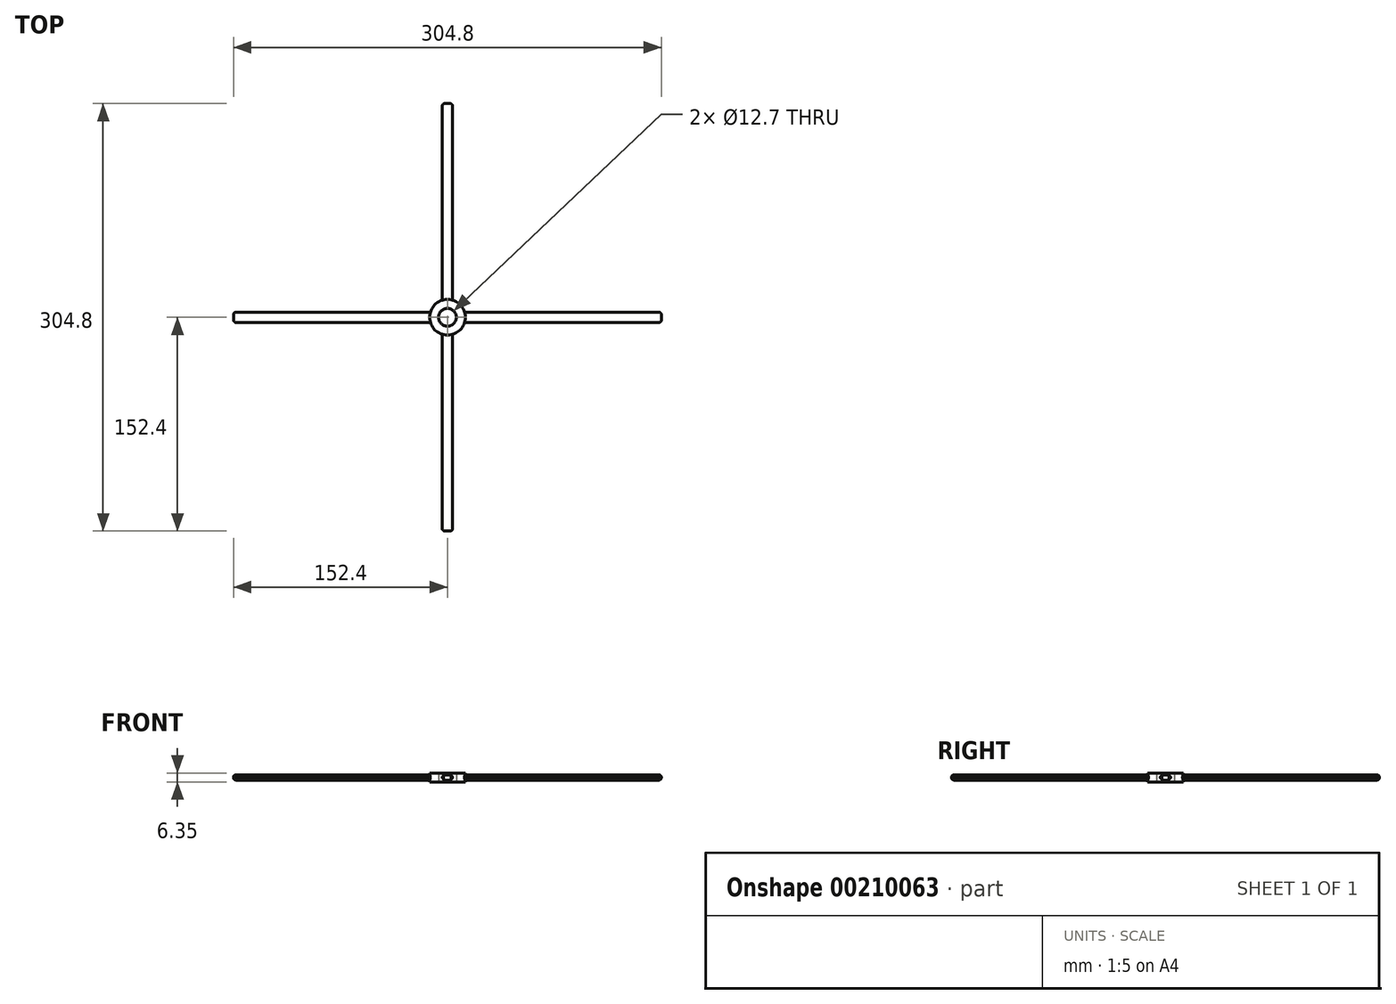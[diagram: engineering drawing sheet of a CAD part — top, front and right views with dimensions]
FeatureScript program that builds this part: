
annotation { "Feature Type Name" : "Feature", "Feature Type Description" : "" }
export const myFeature = defineFeature(function(context is Context, id is Id, definition is map)
    precondition{}
    {
        {
            var Q0;
            Q0=qCreatedBy(makeId("Top.planeOp"),FACE);
            var sketch = newSketch(context, id + "F0", { "sketchPlane" : qUnion([Q0])});
            skCircle(sketch, "E0", {"center": v(0, 0) * mm, "radius": 6.35 * mm});
            skCircle(sketch, "E1", {"center": v(0, 0) * mm, "radius": 12.7 * mm});
            skSolve(sketch);
        }
        {
            var Q0;
            Q0 = qSketchRegion(id + "F0", true);
            extrude(context, id + "F1", {"entities" : qUnion([Q0]), "depth" : 6.35 * mm});
        }
        {
            var Q0;
            Q0=qCreatedBy(makeId("Right.planeOp"),FACE);
            cPlane(context, id + "F2", {"entities" : qUnion([Q0]), "cplaneType" : CPlaneType.OFFSET, "offset" : 152.4 * mm, "width" : 152.4 * mm, "height" : 152.4 * mm});
        }
        {
            var Q0;
            Q0=qCreatedBy(id+"F2.planeOp",FACE);
            var sketch = newSketch(context, id + "F3", { "sketchPlane" : qUnion([Q0])});
            skLineSegment(sketch, "E2", {"start": v(0, 0) * mm, "end": v(12.9, 0) * mm});
            skLineSegment(sketch, "E3", {"start": v(0, 0) * mm, "end": v(0, 15.07) * mm});
            skLineSegment(sketch, "E4.bottom", {"start": v(3.8, 5.08) * mm, "end": v(-3.81, 5.08) * mm});
            skLineSegment(sketch, "E4.top", {"start": v(3.8, 1.27) * mm, "end": v(-3.8, 1.27) * mm});
            skLineSegment(sketch, "E4.left", {"start": v(3.8, 5.08) * mm, "end": v(3.8, 1.27) * mm});
            skLineSegment(sketch, "E4.right", {"start": v(-3.81, 5.08) * mm, "end": v(-3.8, 1.27) * mm});
            skPoint(sketch, "E4.middle", {"position": v(0, 3.18) * mm});
            skSolve(sketch);
        }
        {
            var Q0;
            {var subQ5=sQuery(id+"F3.wireOp",EDGE,"E4.left");Q0=makeQuery(id+"F3.imprint","IMPRINT",FACE,{"disambiguationData":[TD([[makeQuery(id+"F3.imprint","IMPRINT",EDGE,{"derivedFrom":subQ5}),-1.0]])]});}
            var Q1;
            {var subQ5=sQuery(id+"F3.wireOp",EDGE,"E4.right");Q1=makeQuery(id+"F3.imprint","IMPRINT",FACE,{"disambiguationData":[TD([[makeQuery(id+"F3.imprint","IMPRINT",EDGE,{"derivedFrom":subQ5}),1.0]])]});}
            var Q2;
            Q2=makeQuery(id+"F1.opExtrude","SWEPT_FACE",FACE,{"disambiguationData":[OSD([sQuery(id+"F0.wireOp",EDGE,"E1")])]});
            extrude(context, id + "F4", {"entities" : qUnion([Q0, Q1]), "operationType" : NewBodyOperationType.ADD, "endBound" : BoundingType.UP_TO_SURFACE, "oppositeDirection" : true, "endBoundEntityFace" : qUnion([Q2]), "depth" : 25.4 * mm});
        }
        {
            var Q0;
            Q0=makeQuery(id+"F4.opExtrude","SWEPT_EDGE",EDGE,{"disambiguationData":[OSD([sQuery(id+"F3.wireOp",EDGE,"E4.bottom"),sQuery(id+"F3.wireOp",EDGE,"E4.right")])]});
            var Q1;
            Q1=makeQuery(id+"F4.opExtrude","SWEPT_EDGE",EDGE,{"disambiguationData":[OSD([sQuery(id+"F3.wireOp",EDGE,"E4.bottom"),sQuery(id+"F3.wireOp",EDGE,"E4.left")])]});
            var Q2;
            Q2=makeQuery(id+"F4.opExtrude","SWEPT_EDGE",EDGE,{"disambiguationData":[OSD([sQuery(id+"F3.wireOp",EDGE,"E4.top"),sQuery(id+"F3.wireOp",EDGE,"E4.right")])]});
            var Q3;
            Q3=makeQuery(id+"F4.opExtrude","SWEPT_EDGE",EDGE,{"disambiguationData":[OSD([sQuery(id+"F3.wireOp",EDGE,"E4.top"),sQuery(id+"F3.wireOp",EDGE,"E4.left")])]});
            fillet(context, id + "F5", {"entities" : qUnion([Q0, Q1, Q2, Q3]), "radius" : 2.54 * mm, "tangentPropagation" : true, "allowEdgeOverflow" : false});
        }
        {
            var Q0;
            Q0=makeQuery(id+"F4.opExtrude","CAP_EDGE",EDGE,{"disambiguationData":[OSD([sQuery(id+"F3.wireOp",EDGE,"E4.bottom")])],"isStart":true});
            var Q1;
            Q1=makeQuery(id+"F4.opExtrude","CAP_EDGE",EDGE,{"disambiguationData":[OSD([sQuery(id+"F3.wireOp",EDGE,"E4.top")])],"isStart":true});
            var Q2;
            {var subQ0=sQuery(id+"F3.wireOp",EDGE,"E4.right");var subQ1=sQuery(id+"F3.wireOp",EDGE,"E4.top");Q2=makeQuery(id+"F5.opFillet","BLEND_EDGE",EDGE,{"blendedFrom":[makeQuery(id+"F4.opExtrude","SWEPT_EDGE",EDGE,{"disambiguationData":[OSD([subQ1,subQ0])]}),makeQuery(id+"F4.opExtrude","CAP_FACE",FACE,{"disambiguationData":[OSD([sQuery(id+"F3.wireOp",EDGE,"E4.bottom"),subQ1,sQuery(id+"F3.wireOp",EDGE,"E4.left"),subQ0])],"isStart":true})],"blendedInto":[makeQuery(id+"F4.opExtrude","CAP_FACE",FACE,{"disambiguationData":[OSD([sQuery(id+"F3.wireOp",EDGE,"E4.bottom"),subQ1,sQuery(id+"F3.wireOp",EDGE,"E4.left"),subQ0])],"isStart":true})]});}
            var Q3;
            {var subQ0=sQuery(id+"F3.wireOp",EDGE,"E4.right");var subQ1=sQuery(id+"F3.wireOp",EDGE,"E4.bottom");Q3=makeQuery(id+"F5.opFillet","BLEND_EDGE",EDGE,{"blendedFrom":[makeQuery(id+"F4.opExtrude","SWEPT_EDGE",EDGE,{"disambiguationData":[OSD([subQ1,subQ0])]}),makeQuery(id+"F4.opExtrude","CAP_FACE",FACE,{"disambiguationData":[OSD([subQ1,sQuery(id+"F3.wireOp",EDGE,"E4.top"),sQuery(id+"F3.wireOp",EDGE,"E4.left"),subQ0])],"isStart":true})],"blendedInto":[makeQuery(id+"F4.opExtrude","CAP_FACE",FACE,{"disambiguationData":[OSD([subQ1,sQuery(id+"F3.wireOp",EDGE,"E4.top"),sQuery(id+"F3.wireOp",EDGE,"E4.left"),subQ0])],"isStart":true})]});}
            var Q4;
            {var subQ0=sQuery(id+"F3.wireOp",EDGE,"E4.left");var subQ1=sQuery(id+"F3.wireOp",EDGE,"E4.bottom");Q4=makeQuery(id+"F5.opFillet","BLEND_EDGE",EDGE,{"blendedFrom":[makeQuery(id+"F4.opExtrude","SWEPT_EDGE",EDGE,{"disambiguationData":[OSD([subQ1,subQ0])]}),makeQuery(id+"F4.opExtrude","CAP_FACE",FACE,{"disambiguationData":[OSD([subQ1,sQuery(id+"F3.wireOp",EDGE,"E4.top"),subQ0,sQuery(id+"F3.wireOp",EDGE,"E4.right")])],"isStart":true})],"blendedInto":[makeQuery(id+"F4.opExtrude","CAP_FACE",FACE,{"disambiguationData":[OSD([subQ1,sQuery(id+"F3.wireOp",EDGE,"E4.top"),subQ0,sQuery(id+"F3.wireOp",EDGE,"E4.right")])],"isStart":true})]});}
            var Q5;
            {var subQ0=sQuery(id+"F3.wireOp",EDGE,"E4.left");var subQ1=sQuery(id+"F3.wireOp",EDGE,"E4.top");Q5=makeQuery(id+"F5.opFillet","BLEND_EDGE",EDGE,{"blendedFrom":[makeQuery(id+"F4.opExtrude","SWEPT_EDGE",EDGE,{"disambiguationData":[OSD([subQ1,subQ0])]}),makeQuery(id+"F4.opExtrude","CAP_FACE",FACE,{"disambiguationData":[OSD([sQuery(id+"F3.wireOp",EDGE,"E4.bottom"),subQ1,subQ0,sQuery(id+"F3.wireOp",EDGE,"E4.right")])],"isStart":true})],"blendedInto":[makeQuery(id+"F4.opExtrude","CAP_FACE",FACE,{"disambiguationData":[OSD([sQuery(id+"F3.wireOp",EDGE,"E4.bottom"),subQ1,subQ0,sQuery(id+"F3.wireOp",EDGE,"E4.right")])],"isStart":true})]});}
            fillet(context, id + "F6", {"entities" : qUnion([Q0, Q1, Q2, Q3, Q4, Q5]), "radius" : 1.78 * mm, "tangentPropagation" : true, "allowEdgeOverflow" : false});
        }
        {
            var Q0;
            Q0=makeQuery(id+"F1.opExtrude","SWEPT_BODY",BODY,{"disambiguationData":[OSD([sQuery(id+"F0.wireOp",EDGE,"E0"),sQuery(id+"F0.wireOp",EDGE,"E1")])]});
            var Q1;
            Q1=qCreatedBy(makeId("Right.planeOp"),FACE);
            mirror(context, id + "F7", {"operationType" : NewBodyOperationType.ADD, "entities" : qUnion([Q0]), "mirrorPlane" : qUnion([Q1])});
        }
        {
            var Q0;
            Q0=qCreatedBy(makeId("Front.planeOp"),FACE);
            cPlane(context, id + "F8", {"entities" : qUnion([Q0]), "cplaneType" : CPlaneType.OFFSET, "offset" : 152.4 * mm, "oppositeDirection" : true, "width" : 152.4 * mm, "height" : 152.4 * mm});
        }
        {
            var Q0;
            Q0=qCreatedBy(id+"F8.planeOp",FACE);
            var sketch = newSketch(context, id + "F9", { "sketchPlane" : qUnion([Q0])});
            skLineSegment(sketch, "E5", {"start": v(0, 0) * mm, "end": v(-22.85, 0) * mm});
            skLineSegment(sketch, "E6", {"start": v(0, 0) * mm, "end": v(0, 28.61) * mm});
            skLineSegment(sketch, "E7.bottom", {"start": v(-3.81, 5.08) * mm, "end": v(3.8, 5.08) * mm});
            skLineSegment(sketch, "E7.top", {"start": v(-3.81, 1.27) * mm, "end": v(3.8, 1.27) * mm});
            skLineSegment(sketch, "E7.left", {"start": v(-3.81, 5.08) * mm, "end": v(-3.81, 1.27) * mm});
            skLineSegment(sketch, "E7.right", {"start": v(3.8, 5.08) * mm, "end": v(3.8, 1.27) * mm});
            skPoint(sketch, "E7.middle", {"position": v(0, 3.17) * mm});
            skSolve(sketch);
        }
        {
            var Q0;
            {var subQ5=sQuery(id+"F9.wireOp",EDGE,"E7.right");Q0=makeQuery(id+"F9.imprint","IMPRINT",FACE,{"disambiguationData":[TD([[makeQuery(id+"F9.imprint","IMPRINT",EDGE,{"derivedFrom":subQ5}),-1.0]])]});}
            var Q1;
            {var subQ5=sQuery(id+"F9.wireOp",EDGE,"E7.left");Q1=makeQuery(id+"F9.imprint","IMPRINT",FACE,{"disambiguationData":[TD([[makeQuery(id+"F9.imprint","IMPRINT",EDGE,{"derivedFrom":subQ5}),1.0]])]});}
            var Q2;
            Q2=makeQuery(id+"F1.opExtrude","SWEPT_FACE",FACE,{"disambiguationData":[OSD([sQuery(id+"F0.wireOp",EDGE,"E1")])]});
            extrude(context, id + "F10", {"entities" : qUnion([Q0, Q1]), "operationType" : NewBodyOperationType.ADD, "endBound" : BoundingType.UP_TO_SURFACE, "endBoundEntityFace" : qUnion([Q2]), "depth" : 25.4 * mm});
        }
        {
            var Q0;
            Q0=makeQuery(id+"F10.opExtrude","SWEPT_EDGE",EDGE,{"disambiguationData":[OSD([sQuery(id+"F9.wireOp",EDGE,"E7.bottom"),sQuery(id+"F9.wireOp",EDGE,"E7.right")])]});
            var Q1;
            Q1=makeQuery(id+"F10.opExtrude","SWEPT_EDGE",EDGE,{"disambiguationData":[OSD([sQuery(id+"F9.wireOp",EDGE,"E7.top"),sQuery(id+"F9.wireOp",EDGE,"E7.right")])]});
            var Q2;
            Q2=makeQuery(id+"F10.opExtrude","SWEPT_EDGE",EDGE,{"disambiguationData":[OSD([sQuery(id+"F9.wireOp",EDGE,"E7.bottom"),sQuery(id+"F9.wireOp",EDGE,"E7.left")])]});
            var Q3;
            Q3=makeQuery(id+"F10.opExtrude","SWEPT_EDGE",EDGE,{"disambiguationData":[OSD([sQuery(id+"F9.wireOp",EDGE,"E7.top"),sQuery(id+"F9.wireOp",EDGE,"E7.left")])]});
            fillet(context, id + "F11", {"entities" : qUnion([Q0, Q1, Q2, Q3]), "radius" : 2.54 * mm, "tangentPropagation" : true, "allowEdgeOverflow" : false});
        }
        {
            var Q0;
            Q0=makeQuery(id+"F10.opExtrude","CAP_EDGE",EDGE,{"disambiguationData":[OSD([sQuery(id+"F9.wireOp",EDGE,"E7.bottom")])],"isStart":true});
            var Q1;
            Q1=makeQuery(id+"F10.opExtrude","CAP_EDGE",EDGE,{"disambiguationData":[OSD([sQuery(id+"F9.wireOp",EDGE,"E7.top")])],"isStart":true});
            var Q2;
            {var subQ0=sQuery(id+"F9.wireOp",EDGE,"E7.left");var subQ1=sQuery(id+"F9.wireOp",EDGE,"E7.top");Q2=makeQuery(id+"F11.opFillet","BLEND_EDGE",EDGE,{"blendedFrom":[makeQuery(id+"F10.opExtrude","SWEPT_EDGE",EDGE,{"disambiguationData":[OSD([subQ1,subQ0])]}),makeQuery(id+"F10.opExtrude","CAP_FACE",FACE,{"disambiguationData":[OSD([sQuery(id+"F9.wireOp",EDGE,"E7.bottom"),subQ1,subQ0,sQuery(id+"F9.wireOp",EDGE,"E7.right")])],"isStart":true})],"blendedInto":[makeQuery(id+"F10.opExtrude","CAP_FACE",FACE,{"disambiguationData":[OSD([sQuery(id+"F9.wireOp",EDGE,"E7.bottom"),subQ1,subQ0,sQuery(id+"F9.wireOp",EDGE,"E7.right")])],"isStart":true})]});}
            var Q3;
            {var subQ0=sQuery(id+"F9.wireOp",EDGE,"E7.left");var subQ1=sQuery(id+"F9.wireOp",EDGE,"E7.bottom");Q3=makeQuery(id+"F11.opFillet","BLEND_EDGE",EDGE,{"blendedFrom":[makeQuery(id+"F10.opExtrude","SWEPT_EDGE",EDGE,{"disambiguationData":[OSD([subQ1,subQ0])]}),makeQuery(id+"F10.opExtrude","CAP_FACE",FACE,{"disambiguationData":[OSD([subQ1,sQuery(id+"F9.wireOp",EDGE,"E7.top"),subQ0,sQuery(id+"F9.wireOp",EDGE,"E7.right")])],"isStart":true})],"blendedInto":[makeQuery(id+"F10.opExtrude","CAP_FACE",FACE,{"disambiguationData":[OSD([subQ1,sQuery(id+"F9.wireOp",EDGE,"E7.top"),subQ0,sQuery(id+"F9.wireOp",EDGE,"E7.right")])],"isStart":true})]});}
            var Q4;
            {var subQ0=sQuery(id+"F9.wireOp",EDGE,"E7.right");var subQ1=sQuery(id+"F9.wireOp",EDGE,"E7.top");Q4=makeQuery(id+"F11.opFillet","BLEND_EDGE",EDGE,{"blendedFrom":[makeQuery(id+"F10.opExtrude","SWEPT_EDGE",EDGE,{"disambiguationData":[OSD([subQ1,subQ0])]}),makeQuery(id+"F10.opExtrude","CAP_FACE",FACE,{"disambiguationData":[OSD([sQuery(id+"F9.wireOp",EDGE,"E7.bottom"),subQ1,sQuery(id+"F9.wireOp",EDGE,"E7.left"),subQ0])],"isStart":true})],"blendedInto":[makeQuery(id+"F10.opExtrude","CAP_FACE",FACE,{"disambiguationData":[OSD([sQuery(id+"F9.wireOp",EDGE,"E7.bottom"),subQ1,sQuery(id+"F9.wireOp",EDGE,"E7.left"),subQ0])],"isStart":true})]});}
            var Q5;
            {var subQ0=sQuery(id+"F9.wireOp",EDGE,"E7.right");var subQ1=sQuery(id+"F9.wireOp",EDGE,"E7.bottom");Q5=makeQuery(id+"F11.opFillet","BLEND_EDGE",EDGE,{"blendedFrom":[makeQuery(id+"F10.opExtrude","SWEPT_EDGE",EDGE,{"disambiguationData":[OSD([subQ1,subQ0])]}),makeQuery(id+"F10.opExtrude","CAP_FACE",FACE,{"disambiguationData":[OSD([subQ1,sQuery(id+"F9.wireOp",EDGE,"E7.top"),sQuery(id+"F9.wireOp",EDGE,"E7.left"),subQ0])],"isStart":true})],"blendedInto":[makeQuery(id+"F10.opExtrude","CAP_FACE",FACE,{"disambiguationData":[OSD([subQ1,sQuery(id+"F9.wireOp",EDGE,"E7.top"),sQuery(id+"F9.wireOp",EDGE,"E7.left"),subQ0])],"isStart":true})]});}
            fillet(context, id + "F12", {"entities" : qUnion([Q0, Q1, Q2, Q3, Q4, Q5]), "radius" : 1.78 * mm, "tangentPropagation" : true, "allowEdgeOverflow" : false});
        }
        {
            var Q0;
            Q0=makeQuery(id+"F1.opExtrude","SWEPT_BODY",BODY,{"disambiguationData":[OSD([sQuery(id+"F0.wireOp",EDGE,"E0"),sQuery(id+"F0.wireOp",EDGE,"E1")])]});
            var Q1;
            Q1=qCreatedBy(makeId("Front.planeOp"),FACE);
            mirror(context, id + "F13", {"operationType" : NewBodyOperationType.ADD, "entities" : qUnion([Q0]), "mirrorPlane" : qUnion([Q1])});
        }
        {
            var Q0;
            Q0=makeQuery(id+"F1.opExtrude","SWEPT_BODY",BODY,{"disambiguationData":[OSD([sQuery(id+"F0.wireOp",EDGE,"E0"),sQuery(id+"F0.wireOp",EDGE,"E1")])]});
            transform(context, id + "F14", {"entities" : qUnion([Q0]), "transformType" : TransformType.TRANSLATION_3D, "dx" : 0 * mm, "dy" : 0 * mm, "dz" : 0 * mm, "makeCopy" : true});
        }
    });
